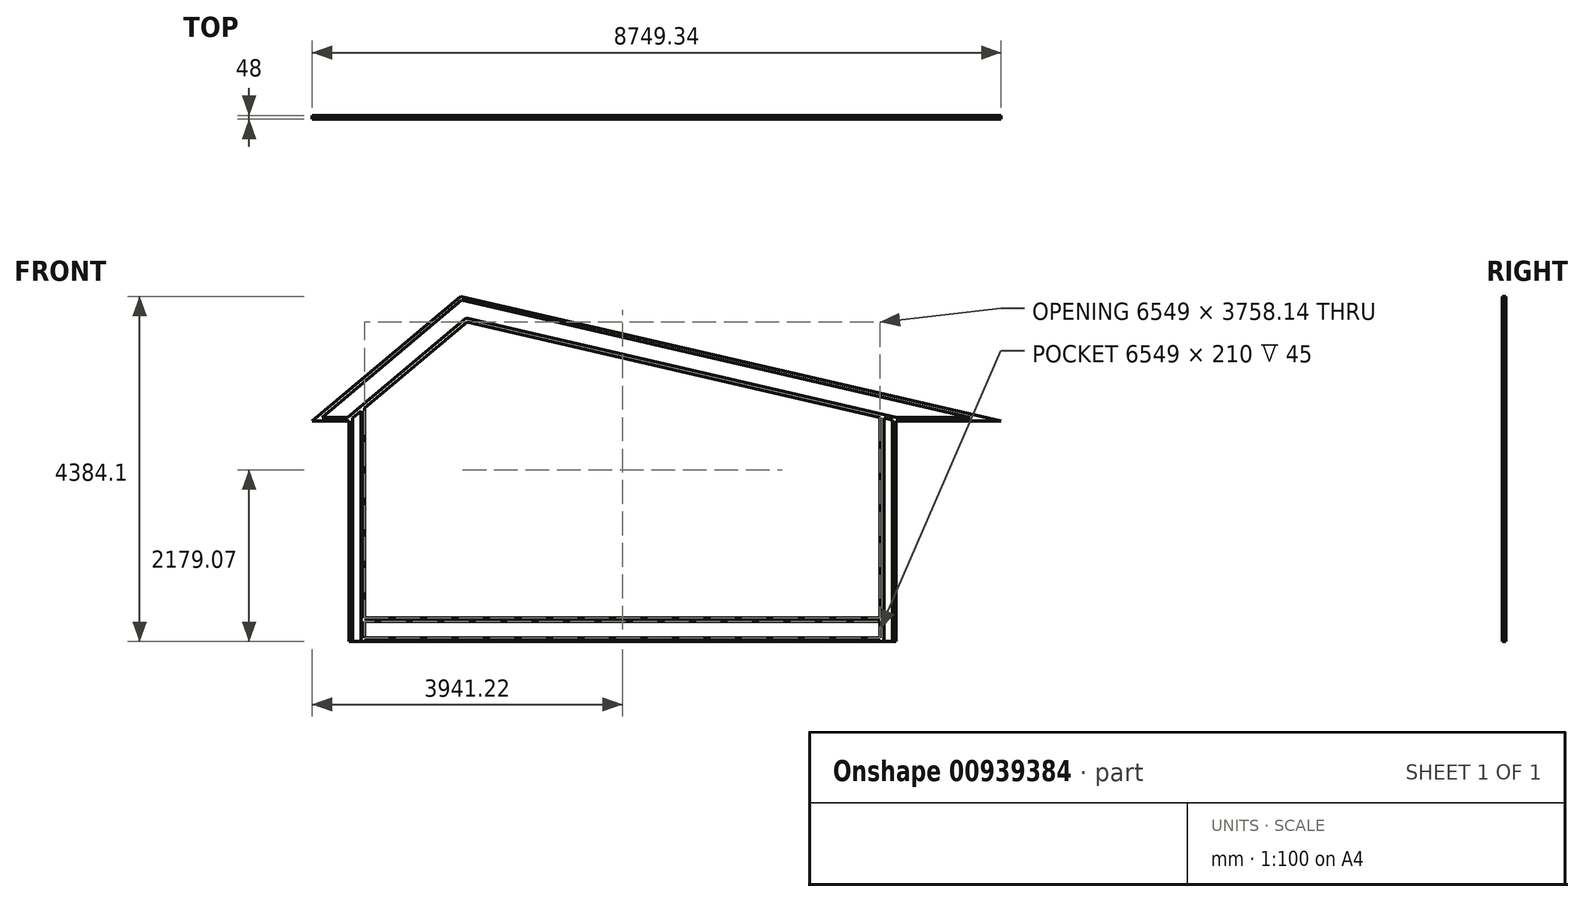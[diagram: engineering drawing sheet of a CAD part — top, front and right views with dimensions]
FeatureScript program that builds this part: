
annotation { "Feature Type Name" : "Feature", "Feature Type Description" : "" }
export const myFeature = defineFeature(function(context is Context, id is Id, definition is map)
    precondition{}
    {
        {
            var Q0;
            Q0=qCreatedBy(makeId("Front.planeOp"),FACE);
            var sketch = newSketch(context, id + "F0", { "sketchPlane" : qUnion([Q0])});
            skLineSegment(sketch, "E0", {"start": v(0, 0) * mm, "end": v(6549, 0) * mm});
            skLineSegment(sketch, "E1", {"start": v(6549, 0) * mm, "end": v(6549, 2546.17) * mm});
            skLineSegment(sketch, "E2", {"start": v(6549, 2546.17) * mm, "end": v(1299.4, 3758.14) * mm});
            skLineSegment(sketch, "E3", {"start": v(1299.4, 3758.14) * mm, "end": v(0, 2667.82) * mm});
            skLineSegment(sketch, "E4", {"start": v(0, 2667.82) * mm, "end": v(0, 0) * mm});
            skLineSegment(sketch, "E5", {"start": v(-200, -300) * mm, "end": v(6749, -300) * mm});
            skLineSegment(sketch, "E6", {"start": v(6749, -300) * mm, "end": v(6749, 2500) * mm});
            skLineSegment(sketch, "E7", {"start": v(1221.14, 4084.1) * mm, "end": v(-666.72, 2500) * mm});
            skLineSegment(sketch, "E8", {"start": v(-666.72, 2500) * mm, "end": v(-200, 2500) * mm});
            skLineSegment(sketch, "E9", {"start": v(-200, 2500) * mm, "end": v(-200, -300) * mm});
            skLineSegment(sketch, "E10", {"start": v(1221.14, 4084.1) * mm, "end": v(8082.62, 2500) * mm});
            skLineSegment(sketch, "E11", {"start": v(8082.62, 2500) * mm, "end": v(6749, 2500) * mm});
            skLineSegment(sketch, "E12", {"start": v(0, 2667.82) * mm, "end": v(-200, 2500) * mm});
            skLineSegment(sketch, "E13", {"start": v(6549, 2546.17) * mm, "end": v(6749, 2500) * mm});
            skSolve(sketch);
        }
        {
            var Q0;
            Q0 = qSketchRegion(id + "F0", true);
            extrude(context, id + "F1", {"entities" : qUnion([Q0]), "depth" : 3 * mm, "offsetDistance" : 25 * mm});
        }
        {
            var Q0;
            Q0=makeQuery(id+"F1.opExtrude","CAP_FACE",FACE,{"disambiguationData":[OSD([sQuery(id+"F0.wireOp",EDGE,"E0"),sQuery(id+"F0.wireOp",EDGE,"E1"),sQuery(id+"F0.wireOp",EDGE,"E2"),sQuery(id+"F0.wireOp",EDGE,"E3"),sQuery(id+"F0.wireOp",EDGE,"E4"),sQuery(id+"F0.wireOp",EDGE,"E5"),sQuery(id+"F0.wireOp",EDGE,"E6"),sQuery(id+"F0.wireOp",EDGE,"E7"),sQuery(id+"F0.wireOp",EDGE,"E8"),sQuery(id+"F0.wireOp",EDGE,"E9"),sQuery(id+"F0.wireOp",EDGE,"E10"),sQuery(id+"F0.wireOp",EDGE,"E11")])],"isStart":false});
            var sketch = newSketch(context, id + "F2", { "sketchPlane" : qUnion([Q0])});
            skLineSegment(sketch, "E14", {"start": v(-596.7, 2500) * mm, "end": v(1232.88, 4035.2) * mm});
            skLineSegment(sketch, "E15", {"start": v(1232.88, 4035.2) * mm, "end": v(7882.58, 2500) * mm});
            skLineSegment(sketch, "E16", {"start": v(1287.66, 3807.03) * mm, "end": v(-270, 2500) * mm});
            skLineSegment(sketch, "E17", {"start": v(1287.66, 3807.03) * mm, "end": v(6949.04, 2500) * mm});
            skLineSegment(sketch, "E18", {"start": v(0, 2667.82) * mm, "end": v(-200, 2500) * mm});
            skLineSegment(sketch, "E19", {"start": v(-200, 2500) * mm, "end": v(-666.72, 2500) * mm});
            skLineSegment(sketch, "E20", {"start": v(-666.72, 2500) * mm, "end": v(1221.14, 4084.1) * mm});
            skLineSegment(sketch, "E21", {"start": v(1221.14, 4084.1) * mm, "end": v(8082.62, 2500) * mm});
            skLineSegment(sketch, "E22", {"start": v(8082.62, 2500) * mm, "end": v(6749, 2500) * mm});
            skLineSegment(sketch, "E23", {"start": v(6749, 2500) * mm, "end": v(6749, -300) * mm});
            skLineSegment(sketch, "E24", {"start": v(6749, -300) * mm, "end": v(-200, -300) * mm});
            skLineSegment(sketch, "E25", {"start": v(-200, -300) * mm, "end": v(-200, 2500) * mm});
            skLineSegment(sketch, "E26", {"start": v(0, 2667.82) * mm, "end": v(0, 0) * mm});
            skLineSegment(sketch, "E27", {"start": v(0, 0) * mm, "end": v(6549, 0) * mm});
            skLineSegment(sketch, "E28", {"start": v(6549, 0) * mm, "end": v(6549, 2546.17) * mm});
            skLineSegment(sketch, "E29", {"start": v(6549, 2546.17) * mm, "end": v(1299.4, 3758.14) * mm});
            skLineSegment(sketch, "E30", {"start": v(1299.4, 3758.14) * mm, "end": v(0, 2667.82) * mm});
            skLineSegment(sketch, "E31", {"start": v(-155, 2537.76) * mm, "end": v(-155, -300) * mm});
            skLineSegment(sketch, "E32", {"start": v(-45, 2630.06) * mm, "end": v(-45, -300) * mm});
            skLineSegment(sketch, "E33", {"start": v(0, 0) * mm, "end": v(0, -300) * mm});
            skLineSegment(sketch, "E34", {"start": v(6549, 2546.17) * mm, "end": v(6749, 2500) * mm});
            skLineSegment(sketch, "E35", {"start": v(6594, 2535.78) * mm, "end": v(6594, -300) * mm});
            skLineSegment(sketch, "E36", {"start": v(6704, -300) * mm, "end": v(6704, 2510.39) * mm});
            skLineSegment(sketch, "E37", {"start": v(6549, 0) * mm, "end": v(6549, -300) * mm});
            skLineSegment(sketch, "E38", {"start": v(6549, -45) * mm, "end": v(0, -45) * mm});
            skLineSegment(sketch, "E39", {"start": v(0, -255) * mm, "end": v(6549, -255) * mm});
            skLineSegment(sketch, "E40", {"start": v(-543.08, 2545) * mm, "end": v(-216.38, 2545) * mm});
            skLineSegment(sketch, "E41", {"start": v(6754.13, 2545) * mm, "end": v(7687.66, 2545) * mm});
            skSolve(sketch);
        }
        {
            var Q0;
            {var subQ0=sQuery(id+"F2.wireOp",EDGE,"E25");Q0=makeQuery(id+"F2.imprint","IMPRINT",FACE,{"disambiguationData":[TD([[makeQuery(id+"F2.imprint","IMPRINT",EDGE,{"derivedFrom":subQ0}),1.0]])]});}
            var Q1;
            {var subQ0=sQuery(id+"F2.wireOp",EDGE,"E23");Q1=makeQuery(id+"F2.imprint","IMPRINT",FACE,{"disambiguationData":[TD([[makeQuery(id+"F2.imprint","IMPRINT",EDGE,{"derivedFrom":subQ0}),1.0]])]});}
            var Q2;
            {var subQ4=sQuery(id+"F2.wireOp",EDGE,"E20");Q2=makeQuery(id+"F2.imprint","IMPRINT",FACE,{"disambiguationData":[TD([[makeQuery(id+"F2.imprint","IMPRINT",EDGE,{"derivedFrom":subQ4}),1.0]])]});}
            var Q3;
            {var subQ3=sQuery(id+"F2.wireOp",EDGE,"E40");Q3=makeQuery(id+"F2.imprint","IMPRINT",FACE,{"disambiguationData":[TD([[makeQuery(id+"F2.imprint","IMPRINT",EDGE,{"derivedFrom":subQ3}),-1.0]])]});}
            var Q4;
            {var subQ3=sQuery(id+"F2.wireOp",EDGE,"E41");Q4=makeQuery(id+"F2.imprint","IMPRINT",FACE,{"disambiguationData":[TD([[makeQuery(id+"F2.imprint","IMPRINT",EDGE,{"derivedFrom":subQ3}),-1.0]])]});}
            var Q5;
            {var subQ5=sQuery(id+"F2.wireOp",EDGE,"E39");Q5=makeQuery(id+"F2.imprint","IMPRINT",FACE,{"disambiguationData":[TD([[makeQuery(id+"F2.imprint","IMPRINT",EDGE,{"derivedFrom":subQ5}),-1.0]])]});}
            var Q6;
            {var subQ4=sQuery(id+"F2.wireOp",EDGE,"E26");Q6=makeQuery(id+"F2.imprint","IMPRINT",FACE,{"disambiguationData":[TD([[makeQuery(id+"F2.imprint","IMPRINT",EDGE,{"derivedFrom":subQ4}),-1.0]])]});}
            var Q7;
            {var subQ1=sQuery(id+"F2.wireOp",EDGE,"E28");Q7=makeQuery(id+"F2.imprint","IMPRINT",FACE,{"disambiguationData":[TD([[makeQuery(id+"F2.imprint","IMPRINT",EDGE,{"derivedFrom":subQ1}),-1.0]])]});}
            var Q8;
            {var subQ6=sQuery(id+"F2.wireOp",EDGE,"E29");Q8=makeQuery(id+"F2.imprint","IMPRINT",FACE,{"disambiguationData":[TD([[makeQuery(id+"F2.imprint","IMPRINT",EDGE,{"derivedFrom":subQ6}),-1.0]])]});}
            var Q9;
            {var subQ0=sQuery(id+"F2.wireOp",EDGE,"E27");Q9=makeQuery(id+"F2.imprint","IMPRINT",FACE,{"disambiguationData":[TD([[makeQuery(id+"F2.imprint","IMPRINT",EDGE,{"derivedFrom":subQ0}),-1.0]])]});}
            extrude(context, id + "F3", {"entities" : qUnion([Q0, Q1, Q2, Q3, Q4, Q5, Q6, Q7, Q8, Q9]), "operationType" : NewBodyOperationType.ADD, "depth" : 45 * mm, "offsetDistance" : 25 * mm});
        }
    });
